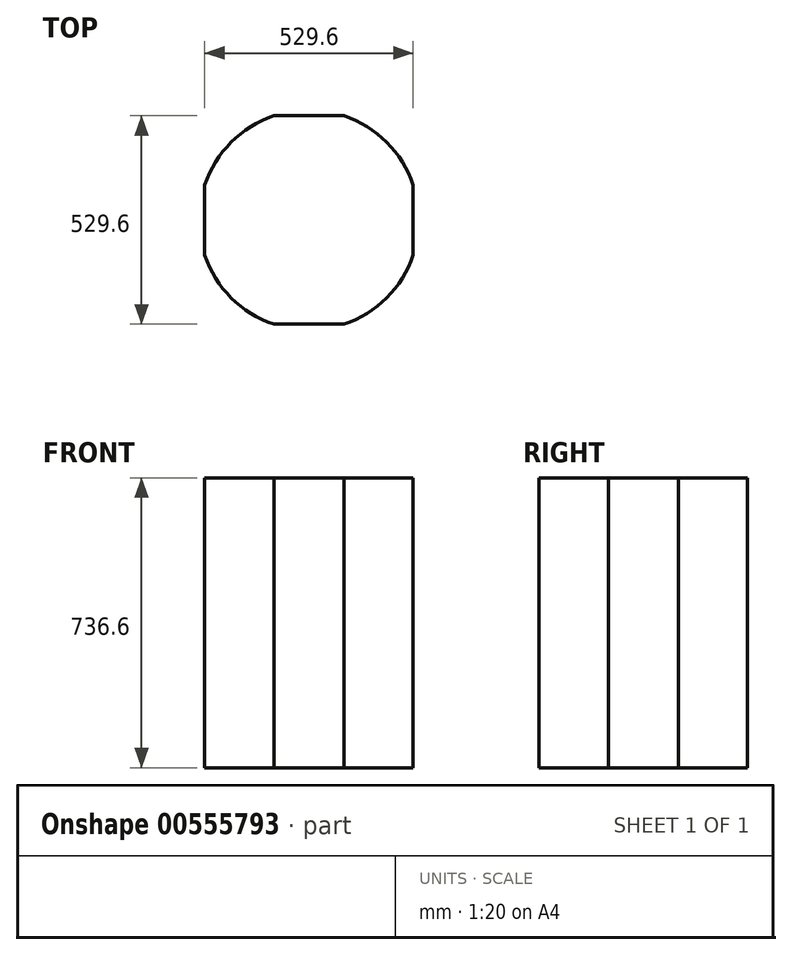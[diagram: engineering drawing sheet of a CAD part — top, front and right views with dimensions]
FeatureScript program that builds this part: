
annotation { "Feature Type Name" : "Feature", "Feature Type Description" : "" }
export const myFeature = defineFeature(function(context is Context, id is Id, definition is map)
    precondition{}
    {
        {
            var Q0;
            Q0=qCreatedBy(makeId("Top.planeOp"),FACE);
            var sketch = newSketch(context, id + "F0", { "sketchPlane" : qUnion([Q0])});
            skCircle(sketch, "E0", {"center": v(0, 0) * mm, "radius": 279.4 * mm});
            skSolve(sketch);
        }
        {
            var Q0;
            Q0 = qSketchRegion(id + "F0", true);
            extrude(context, id + "F1", {"entities" : qUnion([Q0]), "depth" : 736.6 * mm, "offsetDistance" : 25.4 * mm});
        }
        {
            var Q0;
            Q0=qCreatedBy(makeId("Top.planeOp"),FACE);
            var sketch = newSketch(context, id + "F2", { "sketchPlane" : qUnion([Q0])});
            skLineSegment(sketch, "E1.bottom", {"start": v(-97.5, 264.8) * mm, "end": v(98.26, 264.8) * mm});
            skLineSegment(sketch, "E1.top", {"start": v(-97.5, 290.2) * mm, "end": v(98.26, 290.2) * mm});
            skLineSegment(sketch, "E1.left", {"start": v(-97.5, 264.8) * mm, "end": v(-97.5, 290.2) * mm});
            skLineSegment(sketch, "E1.right", {"start": v(98.26, 264.8) * mm, "end": v(98.26, 290.2) * mm});
            skLineSegment(sketch, "E2.1.0", {"start": v(-264.8, -97.5) * mm, "end": v(-264.8, 98.26) * mm});
            skLineSegment(sketch, "E2.1.1", {"start": v(-290.2, -97.5) * mm, "end": v(-290.2, 98.26) * mm});
            skLineSegment(sketch, "E2.1.2", {"start": v(-264.8, 98.26) * mm, "end": v(-290.2, 98.26) * mm});
            skLineSegment(sketch, "E2.1.3", {"start": v(-264.8, -97.5) * mm, "end": v(-290.2, -97.5) * mm});
            skLineSegment(sketch, "E2.2.0", {"start": v(97.5, -264.8) * mm, "end": v(-98.26, -264.8) * mm});
            skLineSegment(sketch, "E2.2.1", {"start": v(97.5, -290.2) * mm, "end": v(-98.26, -290.2) * mm});
            skLineSegment(sketch, "E2.2.2", {"start": v(-98.26, -264.8) * mm, "end": v(-98.26, -290.2) * mm});
            skLineSegment(sketch, "E2.2.3", {"start": v(97.5, -264.8) * mm, "end": v(97.5, -290.2) * mm});
            skLineSegment(sketch, "E2.3.0", {"start": v(264.8, 97.5) * mm, "end": v(264.8, -98.26) * mm});
            skLineSegment(sketch, "E2.3.1", {"start": v(290.2, 97.5) * mm, "end": v(290.2, -98.26) * mm});
            skLineSegment(sketch, "E2.3.2", {"start": v(264.8, -98.26) * mm, "end": v(290.2, -98.26) * mm});
            skLineSegment(sketch, "E2.3.3", {"start": v(264.8, 97.5) * mm, "end": v(290.2, 97.5) * mm});
            skPoint(sketch, "E2.center", {"position": v(0, 0) * mm});
            skSolve(sketch);
        }
        {
            var Q0;
            Q0 = qSketchRegion(id + "F2", true);
            extrude(context, id + "F3", {"entities" : qUnion([Q0]), "operationType" : NewBodyOperationType.REMOVE, "depth" : 1010.92 * mm, "offsetDistance" : 25.4 * mm});
        }
    });
